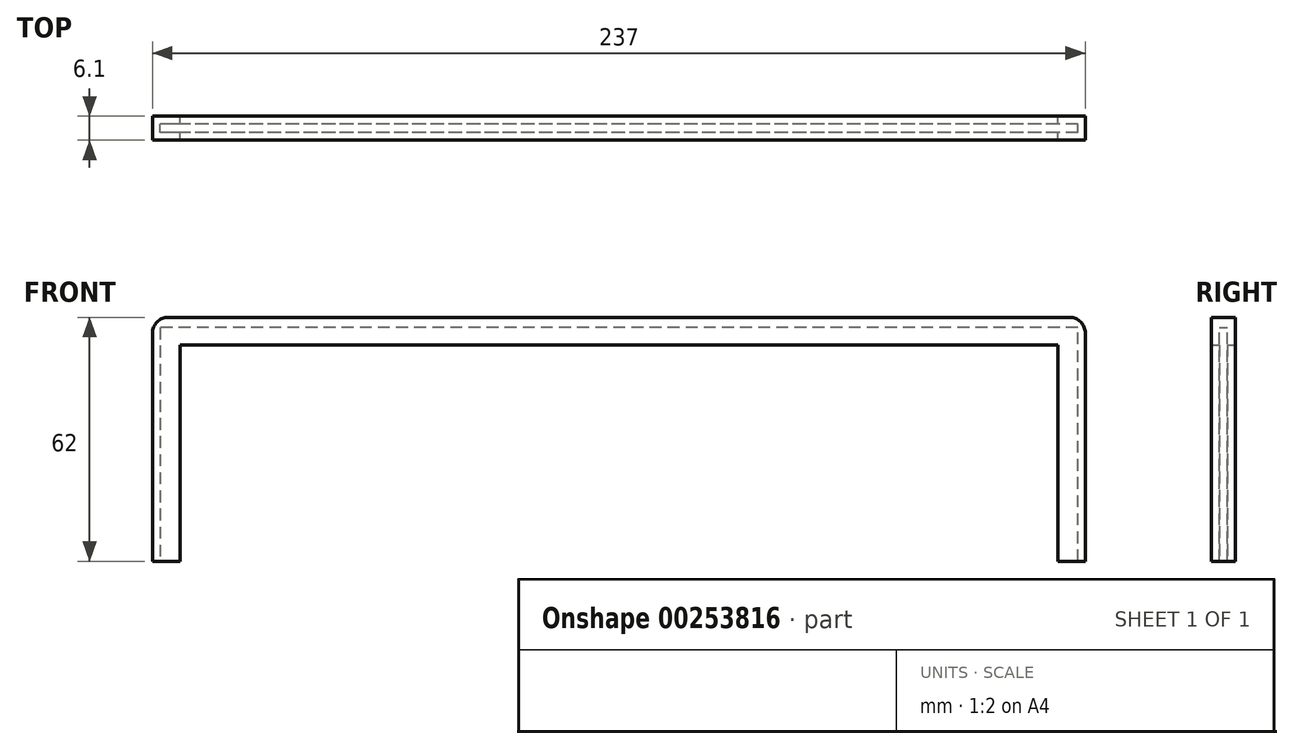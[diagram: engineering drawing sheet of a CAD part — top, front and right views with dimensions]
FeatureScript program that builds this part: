
annotation { "Feature Type Name" : "Feature", "Feature Type Description" : "" }
export const myFeature = defineFeature(function(context is Context, id is Id, definition is map)
    precondition{}
    {
        {
            var Q0;
            Q0=qCreatedBy(makeId("Front.planeOp"),FACE);
            var sketch = newSketch(context, id + "F0", { "sketchPlane" : qUnion([Q0])});
            skLineSegment(sketch, "E0", {"start": v(-118.5, 0) * mm, "end": v(-118.5, 62) * mm});
            skLineSegment(sketch, "E1", {"start": v(-118.5, 62) * mm, "end": v(118.5, 62) * mm});
            skLineSegment(sketch, "E2", {"start": v(118.5, 62) * mm, "end": v(118.5, 0) * mm});
            skLineSegment(sketch, "E3", {"start": v(118.5, 0) * mm, "end": v(111.5, 0) * mm});
            skLineSegment(sketch, "E4", {"start": v(111.5, 0) * mm, "end": v(111.5, 55) * mm});
            skLineSegment(sketch, "E5", {"start": v(111.5, 55) * mm, "end": v(-111.5, 55) * mm});
            skLineSegment(sketch, "E6", {"start": v(-111.5, 55) * mm, "end": v(-111.5, 0) * mm});
            skLineSegment(sketch, "E7", {"start": v(-111.5, 0) * mm, "end": v(-118.5, 0) * mm});
            skSolve(sketch);
        }
        {
            var Q0;
            Q0 = qSketchRegion(id + "F0", true);
            extrude(context, id + "F1", {"entities" : qUnion([Q0]), "depth" : 2 * mm, "offsetDistance" : 25 * mm});
        }
        {
            var Q0;
            Q0=makeQuery(id+"F1.opExtrude","CAP_FACE",FACE,{"disambiguationData":[OSD([sQuery(id+"F0.wireOp",EDGE,"E0"),sQuery(id+"F0.wireOp",EDGE,"E1"),sQuery(id+"F0.wireOp",EDGE,"E2"),sQuery(id+"F0.wireOp",EDGE,"E3"),sQuery(id+"F0.wireOp",EDGE,"E4"),sQuery(id+"F0.wireOp",EDGE,"E5"),sQuery(id+"F0.wireOp",EDGE,"E6"),sQuery(id+"F0.wireOp",EDGE,"E7")])],"isStart":false});
            var sketch = newSketch(context, id + "F2", { "sketchPlane" : qUnion([Q0])});
            skLineSegment(sketch, "E8", {"start": v(-118.5, 0) * mm, "end": v(-118.5, 62) * mm});
            skLineSegment(sketch, "E9", {"start": v(-118.5, 62) * mm, "end": v(118.5, 62) * mm});
            skLineSegment(sketch, "E10", {"start": v(118.5, 62) * mm, "end": v(118.5, 0) * mm});
            skLineSegment(sketch, "E11", {"start": v(118.5, 0) * mm, "end": v(116.6, 0) * mm});
            skLineSegment(sketch, "E12", {"start": v(116.6, 0) * mm, "end": v(116.6, 59.4) * mm});
            skLineSegment(sketch, "E13", {"start": v(116.6, 59.4) * mm, "end": v(-116.6, 59.4) * mm});
            skLineSegment(sketch, "E14", {"start": v(-116.6, 59.4) * mm, "end": v(-116.6, 0) * mm});
            skLineSegment(sketch, "E15", {"start": v(-116.6, 0) * mm, "end": v(-118.5, 0) * mm});
            skSolve(sketch);
        }
        {
            var Q0;
            Q0 = qSketchRegion(id + "F2", true);
            extrude(context, id + "F3", {"entities" : qUnion([Q0]), "operationType" : NewBodyOperationType.ADD, "depth" : 2.1 * mm, "offsetDistance" : 25 * mm});
        }
        {
            var Q0;
            Q0=makeQuery(id+"F3.opExtrude","CAP_FACE",FACE,{"disambiguationData":[OSD([sQuery(id+"F2.wireOp",EDGE,"E8"),sQuery(id+"F2.wireOp",EDGE,"E9"),sQuery(id+"F2.wireOp",EDGE,"E10"),sQuery(id+"F2.wireOp",EDGE,"E11"),sQuery(id+"F2.wireOp",EDGE,"E12"),sQuery(id+"F2.wireOp",EDGE,"E13"),sQuery(id+"F2.wireOp",EDGE,"E14"),sQuery(id+"F2.wireOp",EDGE,"E15")])],"isStart":false});
            var sketch = newSketch(context, id + "F4", { "sketchPlane" : qUnion([Q0])});
            skLineSegment(sketch, "E16", {"start": v(-118.5, 0) * mm, "end": v(-118.5, 62) * mm});
            skLineSegment(sketch, "E17", {"start": v(-118.5, 62) * mm, "end": v(118.5, 62) * mm});
            skLineSegment(sketch, "E18", {"start": v(118.5, 62) * mm, "end": v(118.5, 0) * mm});
            skLineSegment(sketch, "E19", {"start": v(118.5, 0) * mm, "end": v(111.5, 0) * mm});
            skLineSegment(sketch, "E20", {"start": v(111.5, 0) * mm, "end": v(111.5, 55) * mm});
            skLineSegment(sketch, "E21", {"start": v(111.5, 55) * mm, "end": v(-111.5, 55) * mm});
            skLineSegment(sketch, "E22", {"start": v(-111.5, 55) * mm, "end": v(-111.5, 0) * mm});
            skLineSegment(sketch, "E23", {"start": v(-111.5, 0) * mm, "end": v(-118.5, 0) * mm});
            skSolve(sketch);
        }
        {
            var Q0;
            Q0 = qSketchRegion(id + "F4", true);
            extrude(context, id + "F5", {"entities" : qUnion([Q0]), "operationType" : NewBodyOperationType.ADD, "depth" : 2 * mm, "offsetDistance" : 25 * mm});
        }
        {
            var Q0;
            Q0=makeQuery(id+"F5.boolean.opBoolean","MERGE",EDGE,{"derivedFrom":[makeQuery(id+"F3.boolean.opBoolean","MERGE",EDGE,{"derivedFrom":[makeQuery(id+"F1.opExtrude","SWEPT_EDGE",EDGE,{"disambiguationData":[OSD([sQuery(id+"F0.wireOp",EDGE,"E0"),sQuery(id+"F0.wireOp",EDGE,"E1")])]}),makeQuery(id+"F3.opExtrude","SWEPT_EDGE",EDGE,{"disambiguationData":[OSD([sQuery(id+"F2.wireOp",EDGE,"E8"),sQuery(id+"F2.wireOp",EDGE,"E9")])]})]}),makeQuery(id+"F5.opExtrude","SWEPT_EDGE",EDGE,{"disambiguationData":[OSD([sQuery(id+"F4.wireOp",EDGE,"E16"),sQuery(id+"F4.wireOp",EDGE,"E17")])]})]});
            var Q1;
            Q1=makeQuery(id+"F5.boolean.opBoolean","MERGE",EDGE,{"derivedFrom":[makeQuery(id+"F3.boolean.opBoolean","MERGE",EDGE,{"derivedFrom":[makeQuery(id+"F1.opExtrude","SWEPT_EDGE",EDGE,{"disambiguationData":[OSD([sQuery(id+"F0.wireOp",EDGE,"E1"),sQuery(id+"F0.wireOp",EDGE,"E2")])]}),makeQuery(id+"F3.opExtrude","SWEPT_EDGE",EDGE,{"disambiguationData":[OSD([sQuery(id+"F2.wireOp",EDGE,"E9"),sQuery(id+"F2.wireOp",EDGE,"E10")])]})]}),makeQuery(id+"F5.opExtrude","SWEPT_EDGE",EDGE,{"disambiguationData":[OSD([sQuery(id+"F4.wireOp",EDGE,"E17"),sQuery(id+"F4.wireOp",EDGE,"E18")])]})]});
            fillet(context, id + "F6", {"entities" : qUnion([Q0, Q1]), "tangentPropagation" : true, "radius" : 4 * mm, "defaultsChanged" : true, "vertexSettings" : [], "allowEdgeOverflow" : false});
        }
    });
